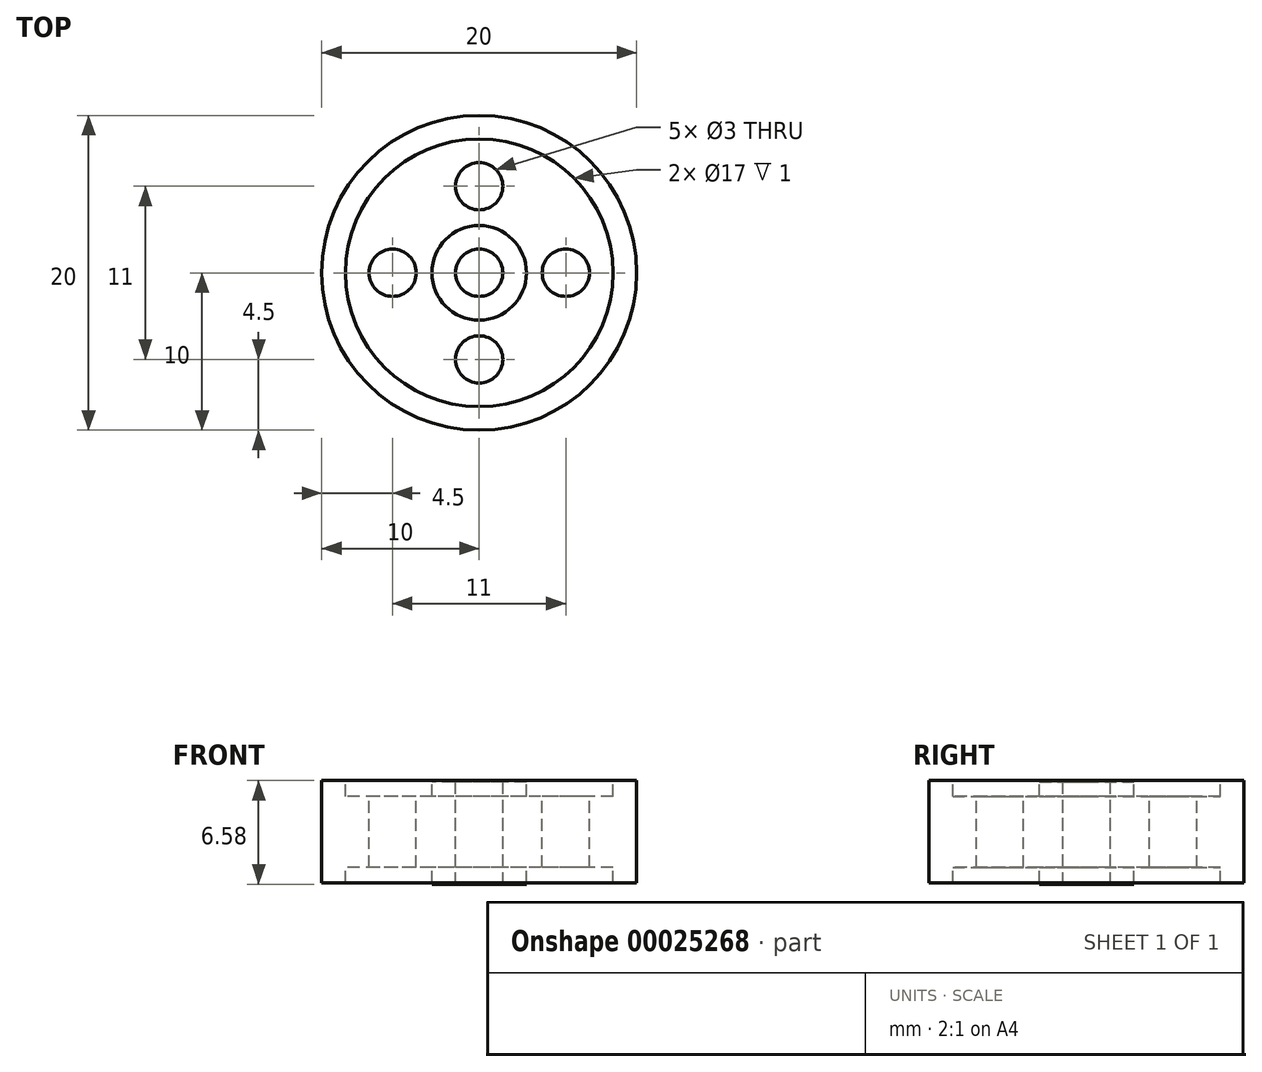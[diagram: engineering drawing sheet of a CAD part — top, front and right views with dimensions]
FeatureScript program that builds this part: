
annotation { "Feature Type Name" : "Feature", "Feature Type Description" : "" }
export const myFeature = defineFeature(function(context is Context, id is Id, definition is map)
    precondition{}
    {
        {
            var Q0;
            Q0=qCreatedBy(makeId("Front.planeOp"),FACE);
            var sketch = newSketch(context, id + "F0", { "sketchPlane" : qUnion([Q0])});
            skLineSegment(sketch, "E0", {"start": v(0, 7.9) * mm, "end": v(0, -7.5) * mm, "construction": true});
            skLineSegment(sketch, "E1.bottom", {"start": v(1.5, 5.09) * mm, "end": v(3, 5.09) * mm});
            skLineSegment(sketch, "E1.top", {"start": v(1.5, -1.41) * mm, "end": v(3, -1.41) * mm});
            skLineSegment(sketch, "E1.left", {"start": v(1.5, 5.09) * mm, "end": v(1.5, -1.41) * mm});
            skLineSegment(sketch, "E1.right", {"start": v(3, 5.09) * mm, "end": v(3, -1.41) * mm});
            skLineSegment(sketch, "E2.bottom", {"start": v(3, -0.33) * mm, "end": v(8.5, -0.33) * mm});
            skLineSegment(sketch, "E2.top", {"start": v(3, 4.17) * mm, "end": v(8.5, 4.17) * mm});
            skLineSegment(sketch, "E2.left", {"start": v(3, 4.17) * mm, "end": v(3, -0.33) * mm});
            skLineSegment(sketch, "E2.right", {"start": v(8.5, 4.17) * mm, "end": v(8.5, -0.33) * mm});
            skLineSegment(sketch, "E3.bottom", {"start": v(8.5, 5.17) * mm, "end": v(10, 5.17) * mm});
            skLineSegment(sketch, "E3.top", {"start": v(8.5, -1.33) * mm, "end": v(10, -1.33) * mm});
            skLineSegment(sketch, "E3.left", {"start": v(8.5, 5.17) * mm, "end": v(8.5, -1.33) * mm});
            skLineSegment(sketch, "E3.right", {"start": v(10, 5.17) * mm, "end": v(10, -1.33) * mm});
            skSolve(sketch);
        }
        {
            var Q0;
            Q0 = qSketchRegion(id + "F0", true);
            var Q1;
            Q1=sQuery(id+"F0.wireOp",EDGE,"E0");
            revolve(context, id + "F1", {"entities" : qUnion([Q0]), "axis" : qUnion([Q1]), "revolveType" : RevolveType.FULL});
        }
        {
            var Q0;
            Q0=makeQuery(id+"F1.opRevolve","SWEPT_FACE",FACE,{"disambiguationData":[OSD([sQuery(id+"F0.wireOp",EDGE,"E2.top")])]});
            var sketch = newSketch(context, id + "F2", { "sketchPlane" : qUnion([Q0])});
            skCircle(sketch, "E4", {"center": v(0, 5.5) * mm, "radius": 1.5 * mm});
            skCircle(sketch, "E5.1.0", {"center": v(-5.5, 0) * mm, "radius": 1.5 * mm});
            skCircle(sketch, "E5.2.0", {"center": v(0, -5.5) * mm, "radius": 1.5 * mm});
            skCircle(sketch, "E5.3.0", {"center": v(5.5, 0) * mm, "radius": 1.5 * mm});
            skPoint(sketch, "E5.center", {"position": v(0, 0) * mm});
            skSolve(sketch);
        }
        {
            var Q0;
            Q0=sQuery(id+"F2.wireOp",VERTEX,"E4.center");
            var Q1;
            Q1=sQuery(id+"F2.wireOp",VERTEX,"E5.3.0.center");
            var Q2;
            Q2=sQuery(id+"F2.wireOp",VERTEX,"E5.2.0.center");
            var Q3;
            Q3=sQuery(id+"F2.wireOp",VERTEX,"E5.1.0.center");
            var Q4;
            Q4=makeQuery(id+"F1.opRevolve","SWEPT_BODY",BODY,{"disambiguationData":[OSD([sQuery(id+"F0.wireOp",EDGE,"E1.bottom"),sQuery(id+"F0.wireOp",EDGE,"E1.top"),sQuery(id+"F0.wireOp",EDGE,"E1.left"),sQuery(id+"F0.wireOp",EDGE,"E1.right"),sQuery(id+"F0.wireOp",EDGE,"E2.bottom"),sQuery(id+"F0.wireOp",EDGE,"E2.top"),sQuery(id+"F0.wireOp",EDGE,"E3.bottom"),sQuery(id+"F0.wireOp",EDGE,"E3.top"),sQuery(id+"F0.wireOp",EDGE,"E3.left"),sQuery(id+"F0.wireOp",EDGE,"E3.right")])]});
            hole(context, id + "F3", {"style" : HoleStyle.SIMPLE, "holeDiameter" : 3 * mm, "endStyle" : HoleEndStyle.THROUGH, "locations" : qUnion([Q0, Q1, Q2, Q3]), "scope" : qUnion([Q4])});
        }
    });
